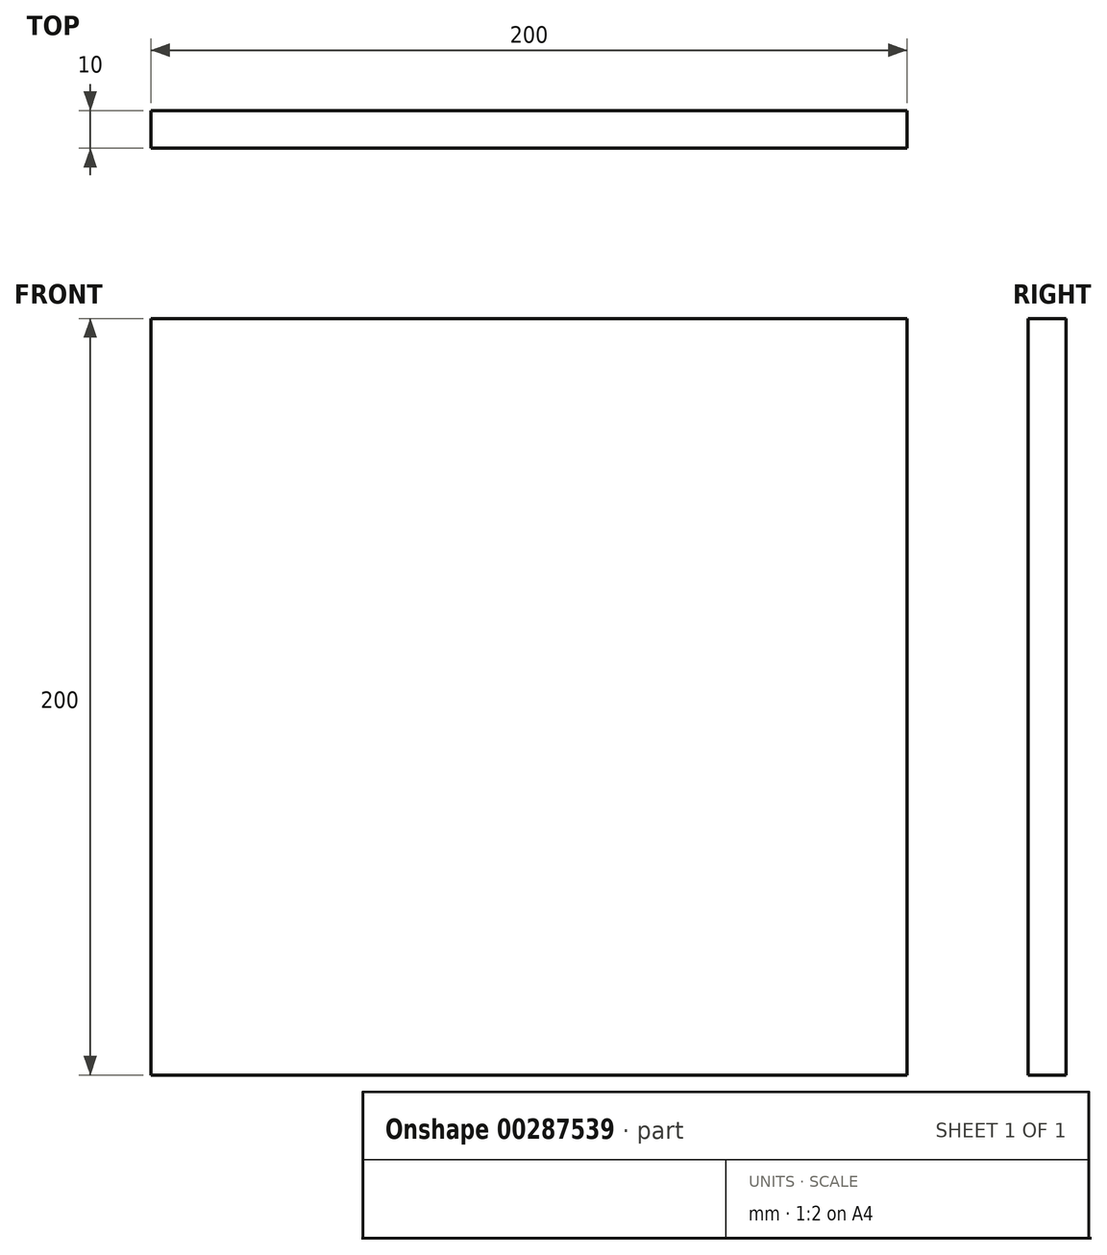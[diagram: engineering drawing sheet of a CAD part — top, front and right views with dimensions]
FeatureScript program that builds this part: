
annotation { "Feature Type Name" : "Feature", "Feature Type Description" : "" }
export const myFeature = defineFeature(function(context is Context, id is Id, definition is map)
    precondition{}
    {
        {
            var Q0;
            Q0=qCreatedBy(makeId("Front.planeOp"),FACE);
            var sketch = newSketch(context, id + "F0", { "sketchPlane" : qUnion([Q0])});
            skLineSegment(sketch, "E0.bottom", {"start": v(-94.34, 154.39) * mm, "end": v(105.66, 154.39) * mm});
            skLineSegment(sketch, "E0.top", {"start": v(-94.34, -45.61) * mm, "end": v(105.66, -45.61) * mm});
            skLineSegment(sketch, "E0.left", {"start": v(-94.34, 154.39) * mm, "end": v(-94.34, -45.61) * mm});
            skLineSegment(sketch, "E0.right", {"start": v(105.66, 154.39) * mm, "end": v(105.66, -45.61) * mm});
            skSolve(sketch);
        }
        {
            var Q0;
            Q0=makeQuery(id+"F0.imprint","IMPRINT",FACE,{"disambiguationData":[TD([[makeQuery(id+"F0.imprint","IMPRINT",EDGE,{"derivedFrom":sQuery(id+"F0.wireOp",EDGE,"E0.bottom")}),-1.0]])]});
            extrude(context, id + "F1", {"entities" : qUnion([Q0]), "depth" : 10 * mm});
        }
    });
